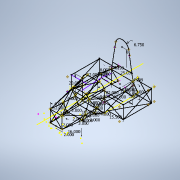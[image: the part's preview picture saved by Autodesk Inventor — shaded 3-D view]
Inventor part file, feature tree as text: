
AUTODESK INVENTOR PART (.ipt)
format: ipt  version: 2021 (Build 250183000, 183)  size: 268,800 bytes
history: native  units: in
note: dims shown in document units (in); Inventor stores cm internally (conversion verified against a paired STEP export)
features: other x46, plane x38, sketch x27
ambient origin geometry x8: Origin, YZ Plane, XZ Plane, XY Plane, X Axis, Y Axis, Z Axis, Center Point
feature tree (111):
  sketch  "Sketch1"  dims[d0=12.0in]
  plane  "Work Plane1"
  sketch  "Sketch2"  dims[d1=12.0in]
  plane  "Work Plane2"
  plane  "Work Plane3"
  sketch  "Sketch3"  dims[d2=2.0in]
  plane  "Work Plane4"
  plane  "Work Plane5"
  plane  "Work Plane6"
  plane  "Work Plane7"
  plane  "Work Plane8"
  plane  "Work Plane9"
  other  "Work Point1"
  other  "Work Point2"
  other  "Work Point3"
  other  "Work Point4"
  other  "Work Point5"
  other  "Work Point6"
  other  "Work Point7"
  other  "Work Point8"
  other  "Work Point9"
  other  "Work Point10"
  other  "Work Point11"
  other  "Work Point12"
  other  "Work Point13"
  other  "Work Point14"
  other  "Work Point15"
  other  "Work Point16"
  other  "Work Point17"
  other  "Work Point18"
  other  "Work Point19"
  other  "Work Point20"
  other  "Work Point21"
  other  "Work Point22"
  other  "Work Point23"
  other  "Work Point24"
  other  "Work Point27"
  other  "Work Point28"
  other  "Work Point29"
  other  "Work Point30"
  other  "Work Point31"
  other  "Work Point32"
  other  "Work Point33"
  other  "Work Point34"
  other  "Work Point35"
  other  "Work Point36"
  other  "Work Point38"
  other  "Work Point40"
  other  "Work Point41"
  other  "Work Point42"
  other  "Work Point43"
  other  "Work Point44"
  plane  "Work Plane10"
  sketch  "Sketch11"  dims[d3=-18.5in]
  plane  "Work Plane11"
  sketch  "Sketch12"  dims[d4=16.0in]
  plane  "Work Plane12"
  sketch  "Sketch13"  dims[d5=2.0in]
  plane  "Work Plane13"
  sketch  "Sketch14"  dims[d6=3.0in]
  plane  "Work Plane14"
  sketch  "Sketch15"  dims[d7=6.0in]
  plane  "Work Plane15"
  sketch  "Sketch16"  dims[d8=3.0in]
  plane  "Work Plane16"
  sketch  "Sketch17"  dims[d9=6.0in]
  plane  "Work Plane17"
  sketch  "Sketch18"  dims[d10=-6.0in d11=-6.0in]
  other  "Work Point55"
  other  "Work Point56"
  other  "Work Point57"
  other  "Work Point58"
  plane  "Work Plane18"
  sketch  "Sketch19"  dims[d12=16.0in]
  plane  "Work Plane19"
  sketch  "Sketch20"  dims[d13=2.0in]
  plane  "Work Plane20"
  sketch  "Sketch21"  dims[d14=3.0in]
  plane  "Work Plane21"
  sketch  "Sketch22"  dims[d15=3.0in]
  plane  "Work Plane22"
  sketch  "Sketch23"  dims[d16=6.0in]
  plane  "Work Plane23"
  sketch  "Sketch24"  dims[d17=6.0in]
  plane  "Work Plane24"
  sketch  "Sketch25"  dims[d18=-7.5in]
  plane  "Work Plane25"
  sketch  "Sketch26"  dims[d19=22.0in]
  plane  "Work Plane26"
  sketch  "Sketch27"  dims[d21=20.0in]
  plane  "Work Plane27"
  sketch  "Sketch28"  dims[d23=12.0in]
  plane  "Work Plane28"
  sketch  "Sketch29"  dims[d24=25.0in]
  plane  "Work Plane29"
  plane  "Work Plane36"
  plane  "Work Plane37"
  plane  "Work Plane39"
  plane  "Work Plane53"
  sketch  "Sketch41"  dims[d26=13.0in]
  plane  "Work Plane41"
  sketch  "Sketch42"  dims[d31=-29.4in]
  plane  "Work Plane43"
  sketch  "Sketch44"  dims[d32=22.0in]
  plane  "Work Plane44"
  other  "Work Point63"
  other  "Work Point64"
  plane  "Work Plane50"
  sketch  "Sketch51"  dims[d33=13.0in d34=13.0in d42=6.75in d43=25.036in d45=-6.0in d52=-7.5in d58=-6.0in d61=-6.0in d67=9.8in d68=9.8in d69=22.0in d85=7.0in d105=4.299in d109=0.0831in d110=8.0in d113=8.0in d114=4.299in d116=0.0831in d118=0.5in d122=3.5483in d124=15.5in d125=4.0in d126=2.0in d127=2.0in d128=2.0in d129=2.0in d130=2.0in d131=2.0in d132=2.0in d133=2.0in]
  plane  "Work Plane56"
  sketch  "3D Sketch1"
